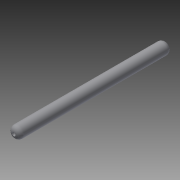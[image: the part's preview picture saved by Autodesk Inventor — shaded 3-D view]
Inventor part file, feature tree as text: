
AUTODESK INVENTOR PART (.ipt)
format: ipt  version: 2014 SP1 (Build 180222100, 222)  size: 82,432 bytes
history: native  units: in
note: dims shown in document units (in); Inventor stores cm internally (conversion verified against a paired STEP export)
features: extrude x1, fillet x1, sketch x1
ambient origin geometry x8: Origin, YZ Plane, XZ Plane, XY Plane, X Axis, Y Axis, Z Axis, Center Point
bodies: Solid1 (feature_tree)
feature tree (3):
  extrude  "Extrusion1"  Depth=1.0in
  fillet  "Fillet1"  Radius=32.0in
  sketch  "Sketch1"  dims[d0=2.5in d1=0.75in d2=32.0in d3=0.0in d4=1.0in]
